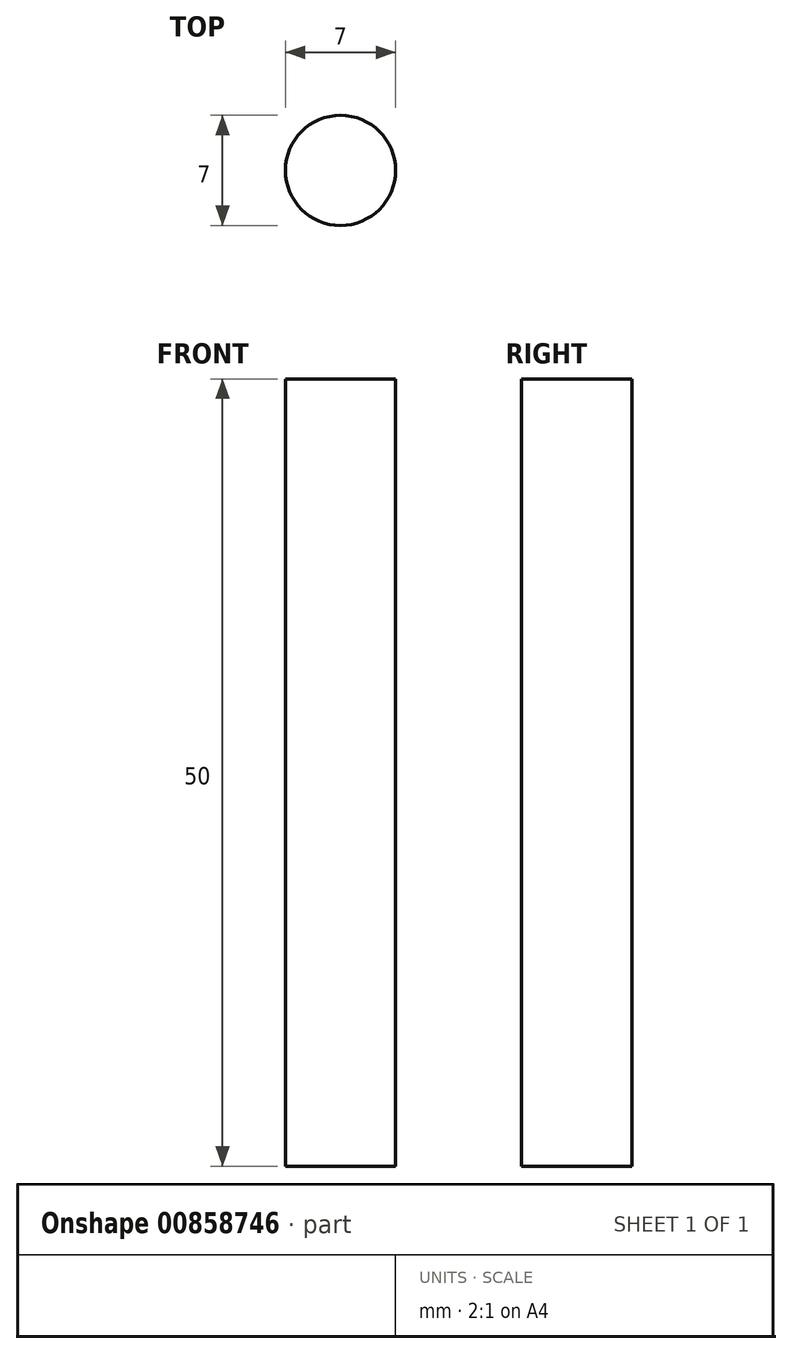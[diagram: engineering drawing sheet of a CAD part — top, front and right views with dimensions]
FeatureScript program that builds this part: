
annotation { "Feature Type Name" : "Feature", "Feature Type Description" : "" }
export const myFeature = defineFeature(function(context is Context, id is Id, definition is map)
    precondition{}
    {
        {
            var Q0;
            Q0=qCreatedBy(makeId("Top.planeOp"),FACE);
            var sketch = newSketch(context, id + "F0", { "sketchPlane" : qUnion([Q0])});
            skCircle(sketch, "E0", {"center": v(0, 0) * mm, "radius": 3.5 * mm});
            skSolve(sketch);
        }
        {
            var Q0;
            Q0 = qSketchRegion(id + "F0", true);
            extrude(context, id + "F1", {"entities" : qUnion([Q0]), "depth" : 50 * mm, "offsetDistance" : 25 * mm});
        }
    });
